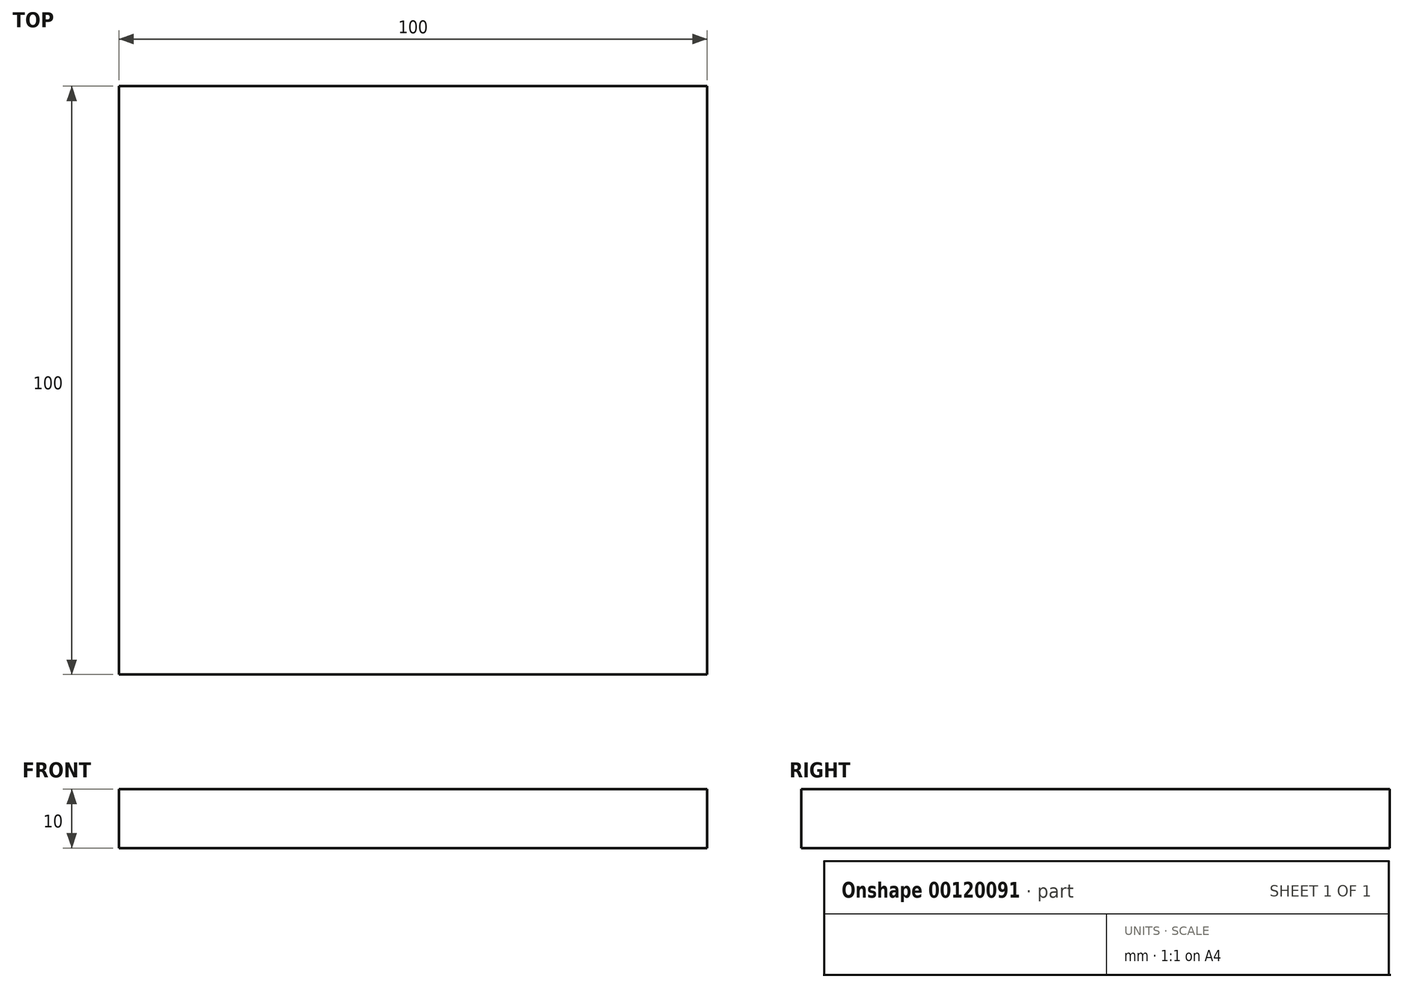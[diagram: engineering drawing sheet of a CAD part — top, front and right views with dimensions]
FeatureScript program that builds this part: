
annotation { "Feature Type Name" : "Feature", "Feature Type Description" : "" }
export const myFeature = defineFeature(function(context is Context, id is Id, definition is map)
    precondition{}
    {
        {
            var Q0;
            Q0=qCreatedBy(makeId("Top.planeOp"),FACE);
            var sketch = newSketch(context, id + "F0", { "sketchPlane" : qUnion([Q0])});
            skLineSegment(sketch, "E0.bottom", {"start": v(-50, -50) * mm, "end": v(50, -50) * mm});
            skLineSegment(sketch, "E0.top", {"start": v(-50, 50) * mm, "end": v(50, 50) * mm});
            skLineSegment(sketch, "E0.left", {"start": v(-50, -50) * mm, "end": v(-50, 50) * mm});
            skLineSegment(sketch, "E0.right", {"start": v(50, -50) * mm, "end": v(50, 50) * mm});
            skPoint(sketch, "E0.middle", {"position": v(0, 0) * mm});
            skSolve(sketch);
        }
        {
            var Q0;
            Q0 = qSketchRegion(id + "F0", true);
            extrude(context, id + "F1", {"entities" : qUnion([Q0]), "endBound" : BoundingType.SYMMETRIC, "depth" : 10 * mm});
        }
    });
